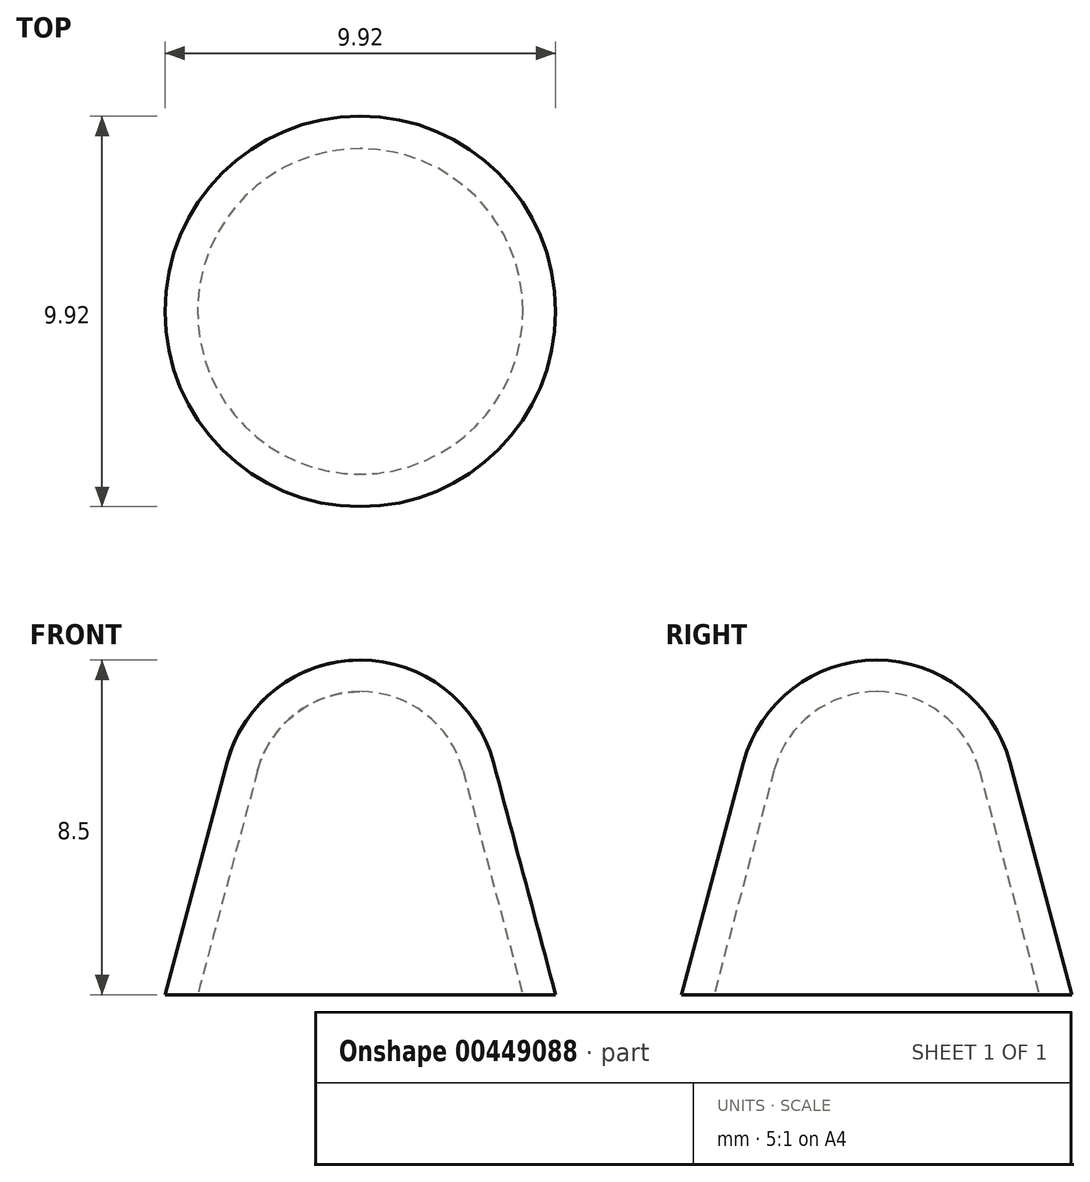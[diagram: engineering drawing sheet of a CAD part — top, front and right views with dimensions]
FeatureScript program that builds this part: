
annotation { "Feature Type Name" : "Feature", "Feature Type Description" : "" }
export const myFeature = defineFeature(function(context is Context, id is Id, definition is map)
    precondition{}
    {
        {
            var Q0;
            Q0=qCreatedBy(makeId("Front.planeOp"),FACE);
            var sketch = newSketch(context, id + "F0", { "sketchPlane" : qUnion([Q0])});
            skCircle(sketch, "E0", {"center": v(0, 0) * mm, "radius": 3.5 * mm, "construction": true});
            skLineSegment(sketch, "E1", {"start": v(-4.96, -5) * mm, "end": v(4.96, -5) * mm});
            skPoint(sketch, "E2", {"position": v(0, -5) * mm});
            skLineSegment(sketch, "E3", {"start": v(-4.96, -5) * mm, "end": v(-3.38, 0.9) * mm});
            skLineSegment(sketch, "E4", {"start": v(4.96, -5) * mm, "end": v(3.38, 0.9) * mm});
            skArc(sketch, "E5", {"start": v(3.38, 0.9) * mm, "mid": v(0, 3.5) * mm, "end": v(-3.38, 0.9) * mm});
            skLineSegment(sketch, "E6", {"start": v(0, 3.5) * mm, "end": v(0, -5) * mm});
            skSolve(sketch);
        }
        {
            var Q0;
            {var subQ0=sQuery(id+"F0.wireOp",EDGE,"E3");Q0=makeQuery(id+"F0.imprint","IMPRINT",FACE,{"disambiguationData":[TD([[makeQuery(id+"F0.imprint","IMPRINT",EDGE,{"derivedFrom":subQ0}),-1.0]])]});}
            var Q1;
            Q1=sQuery(id+"F0.wireOp",EDGE,"E6");
            revolve(context, id + "F1", {"entities" : qUnion([Q0]), "axis" : qUnion([Q1]), "revolveType" : RevolveType.FULL});
        }
        {
            var Q0;
            Q0=makeQuery(id+"F1.opRevolve","SWEPT_FACE",FACE,{"disambiguationData":[OSD([sQuery(id+"F0.wireOp",EDGE,"E1")])]});
            shell(context, id + "F2", {"entities" : qUnion([Q0]), "thickness" : 0.8 * mm});
        }
    });
